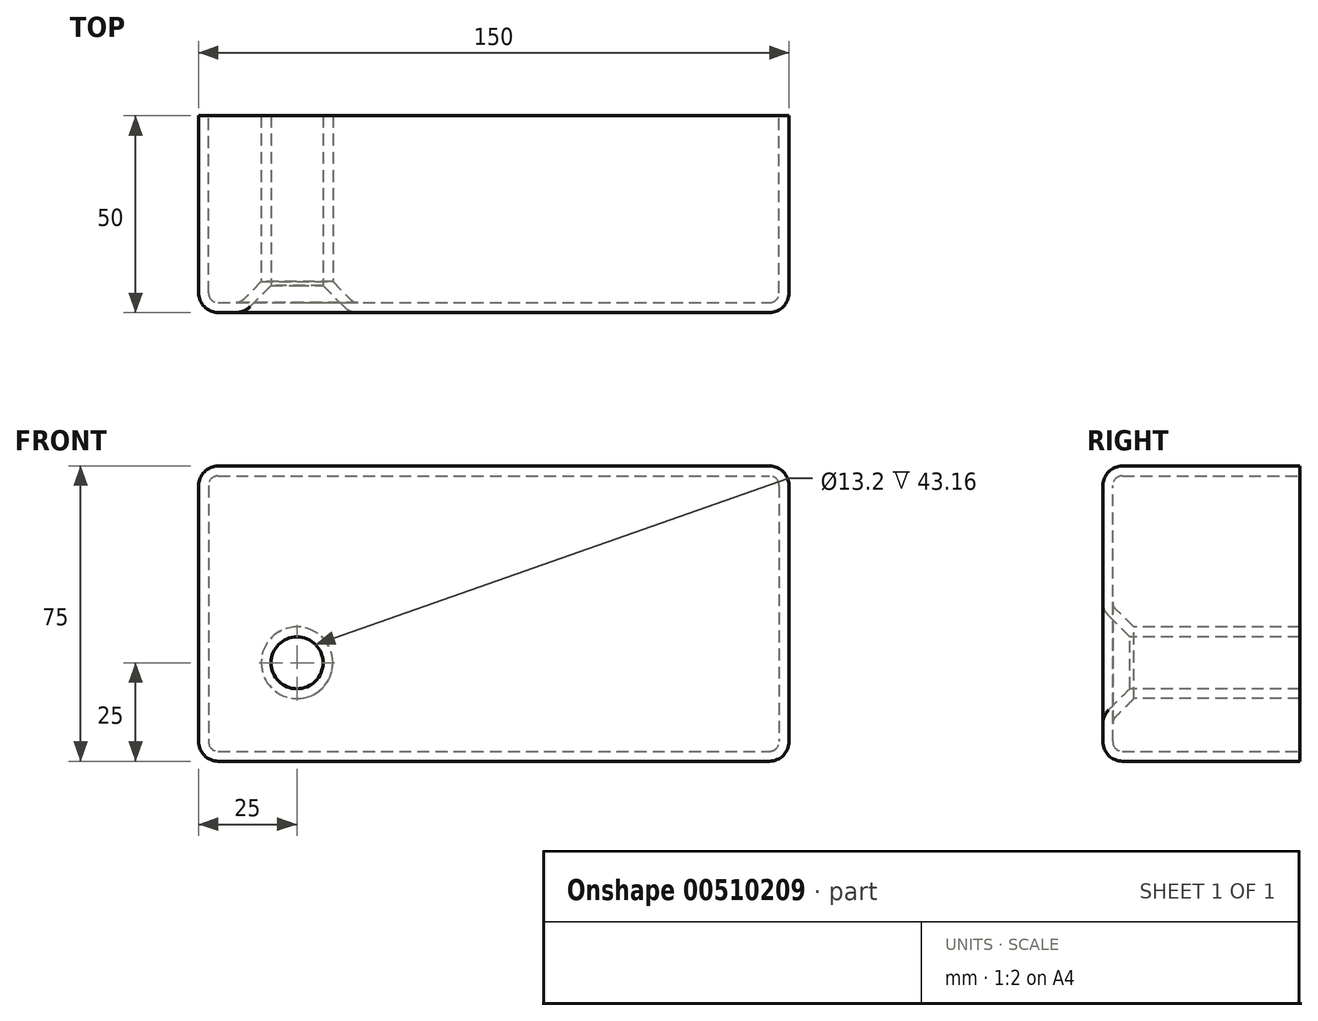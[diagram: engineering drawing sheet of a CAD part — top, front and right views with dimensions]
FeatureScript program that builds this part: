
annotation { "Feature Type Name" : "Feature", "Feature Type Description" : "" }
export const myFeature = defineFeature(function(context is Context, id is Id, definition is map)
    precondition{}
    {
        {
            var Q0;
            Q0=qCreatedBy(makeId("Top.planeOp"),FACE);
            var sketch = newSketch(context, id + "F0", { "sketchPlane" : qUnion([Q0])});
            skLineSegment(sketch, "E0.bottom", {"start": v(0, 0) * mm, "end": v(150, 0) * mm});
            skLineSegment(sketch, "E0.top", {"start": v(0, 50) * mm, "end": v(150, 50) * mm});
            skLineSegment(sketch, "E0.left", {"start": v(0, 0) * mm, "end": v(0, 50) * mm});
            skLineSegment(sketch, "E0.right", {"start": v(150, 0) * mm, "end": v(150, 50) * mm});
            skSolve(sketch);
        }
        {
            var Q0;
            Q0=makeQuery(id+"F0.imprint","IMPRINT",FACE,{"disambiguationData":[TD([[makeQuery(id+"F0.imprint","IMPRINT",EDGE,{"derivedFrom":sQuery(id+"F0.wireOp",EDGE,"E0.bottom")}),1.0]])]});
            extrude(context, id + "F1", {"entities" : qUnion([Q0]), "depth" : 75 * mm});
        }
        {
            var Q0;
            Q0=makeQuery(id+"F1.opExtrude","SWEPT_FACE",FACE,{"disambiguationData":[OSD([sQuery(id+"F0.wireOp",EDGE,"E0.bottom")])]});
            var sketch = newSketch(context, id + "F2", { "sketchPlane" : qUnion([Q0])});
            skPoint(sketch, "E1", {"position": v(25, 25) * mm});
            skSolve(sketch);
        }
        {
            var Q0;
            Q0=sQuery(id+"F2.wireOp",VERTEX,"E1");
            var Q1;
            Q1=makeQuery(id+"F1.opExtrude","SWEPT_BODY",BODY,{"disambiguationData":[OSD([sQuery(id+"F0.wireOp",EDGE,"E0.bottom"),sQuery(id+"F0.wireOp",EDGE,"E0.top"),sQuery(id+"F0.wireOp",EDGE,"E0.left"),sQuery(id+"F0.wireOp",EDGE,"E0.right")])]});
            hole(context, id + "F3", {"style" : HoleStyle.C_SINK, "endStyle" : HoleEndStyle.THROUGH, "standardTappedOrClearance" : lookupTablePath({ "standard" : "ISO", "fit" : "Normal", "size" : "M12", "type" : "Clearance" }), "standardBlindInLast" : lookupTablePath({ "fit" : "Standard", "standard" : "ISO", "size" : "M12", "type" : "Clearance" }), "holeDiameter" : 13.2 * mm, "cSinkDiameter" : 26.88 * mm, "cSinkAngle" : 90 * degree, "isTappedThrough" : true, "tappedDepth" : 12 * mm, "tapClearance" : 3, "startFromSketch" : true, "locations" : qUnion([Q0]), "scope" : qUnion([Q1])});
        }
        {
            var Q0;
            Q0=makeQuery(id+"F1.opExtrude","CAP_EDGE",EDGE,{"disambiguationData":[OSD([sQuery(id+"F0.wireOp",EDGE,"E0.right")])],"isStart":false});
            var Q1;
            Q1=makeQuery(id+"F1.opExtrude","CAP_EDGE",EDGE,{"disambiguationData":[OSD([sQuery(id+"F0.wireOp",EDGE,"E0.right")])],"isStart":true});
            var Q2;
            Q2=makeQuery(id+"F1.opExtrude","CAP_EDGE",EDGE,{"disambiguationData":[OSD([sQuery(id+"F0.wireOp",EDGE,"E0.left")])],"isStart":true});
            var Q3;
            Q3=makeQuery(id+"F1.opExtrude","CAP_EDGE",EDGE,{"disambiguationData":[OSD([sQuery(id+"F0.wireOp",EDGE,"E0.left")])],"isStart":false});
            fillet(context, id + "F4", {"entities" : qUnion([Q0, Q1, Q2, Q3]), "radius" : 5 * mm, "tangentPropagation" : true, "allowEdgeOverflow" : false});
        }
        {
            var Q0;
            Q0=makeQuery(id+"F1.opExtrude","SWEPT_FACE",FACE,{"disambiguationData":[OSD([sQuery(id+"F0.wireOp",EDGE,"E0.bottom")])]});
            fillet(context, id + "F5", {"entities" : qUnion([Q0]), "radius" : 5 * mm, "tangentPropagation" : true, "allowEdgeOverflow" : false});
        }
        {
            var Q0;
            Q0=makeQuery(id+"F1.opExtrude","SWEPT_FACE",FACE,{"disambiguationData":[OSD([sQuery(id+"F0.wireOp",EDGE,"E0.top")])]});
            shell(context, id + "F6", {"entities" : qUnion([Q0]), "thickness" : 2.5 * mm});
        }
    });
